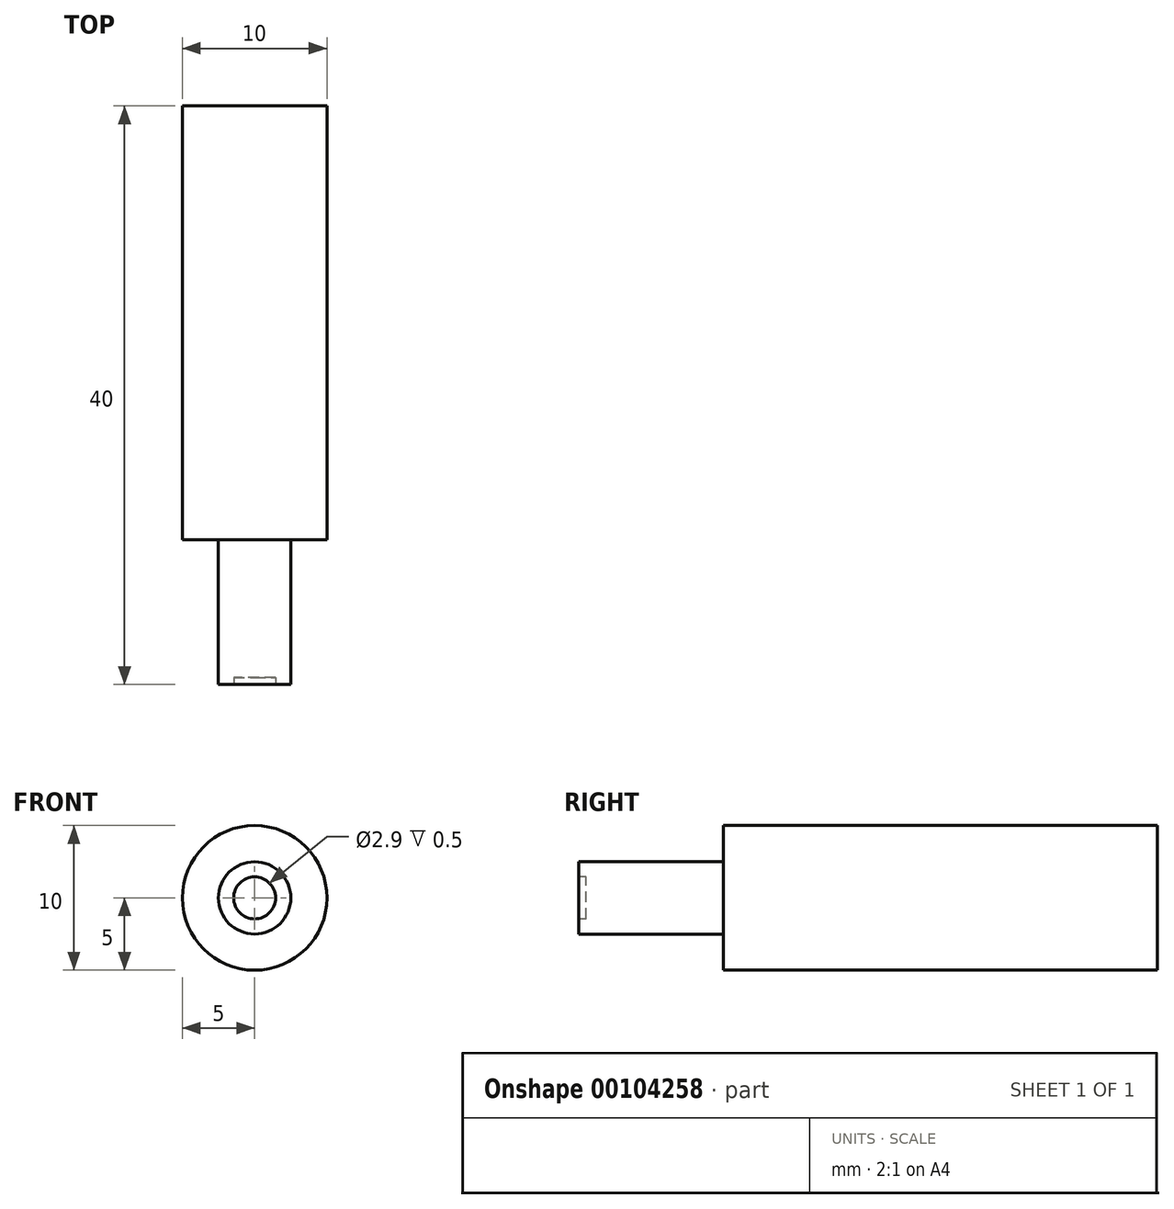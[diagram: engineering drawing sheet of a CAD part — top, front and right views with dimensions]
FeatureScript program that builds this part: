
annotation { "Feature Type Name" : "Feature", "Feature Type Description" : "" }
export const myFeature = defineFeature(function(context is Context, id is Id, definition is map)
    precondition{}
    {
        {
            var Q0;
            Q0=qCreatedBy(makeId("Front.planeOp"),FACE);
            var sketch = newSketch(context, id + "F0", { "sketchPlane" : qUnion([Q0])});
            skCircle(sketch, "E0", {"center": v(0, 0) * mm, "radius": 5 * mm});
            skSolve(sketch);
        }
        {
            var Q0;
            Q0 = qSketchRegion(id + "F0", true);
            extrude(context, id + "F1", {"entities" : qUnion([Q0]), "depth" : 40 * mm});
        }
        {
            var Q0;
            Q0=makeQuery(id+"F1.opExtrude","CAP_FACE",FACE,{"disambiguationData":[OSD([sQuery(id+"F0.wireOp",EDGE,"E0")])],"isStart":false});
            var sketch = newSketch(context, id + "F2", { "sketchPlane" : qUnion([Q0])});
            skCircle(sketch, "E1", {"center": v(0, 0) * mm, "radius": 2.5 * mm});
            skCircle(sketch, "E2", {"center": v(0, 0) * mm, "radius": 5.5 * mm});
            skSolve(sketch);
        }
        {
            var Q0;
            Q0 = qSketchRegion(id + "F2", true);
            extrude(context, id + "F3", {"entities" : qUnion([Q0]), "operationType" : NewBodyOperationType.REMOVE, "oppositeDirection" : true, "depth" : 10 * mm});
        }
        {
            var Q0;
            Q0=makeQuery(id+"F1.opExtrude","CAP_FACE",FACE,{"disambiguationData":[OSD([sQuery(id+"F0.wireOp",EDGE,"E0")])],"isStart":false});
            var sketch = newSketch(context, id + "F4", { "sketchPlane" : qUnion([Q0])});
            skCircle(sketch, "E3", {"center": v(0, 0) * mm, "radius": 1.45 * mm});
            skSolve(sketch);
        }
        {
            var Q0;
            Q0 = qSketchRegion(id + "F4", true);
            extrude(context, id + "F5", {"entities" : qUnion([Q0]), "operationType" : NewBodyOperationType.REMOVE, "oppositeDirection" : true, "depth" : 0.5 * mm});
        }
    });
